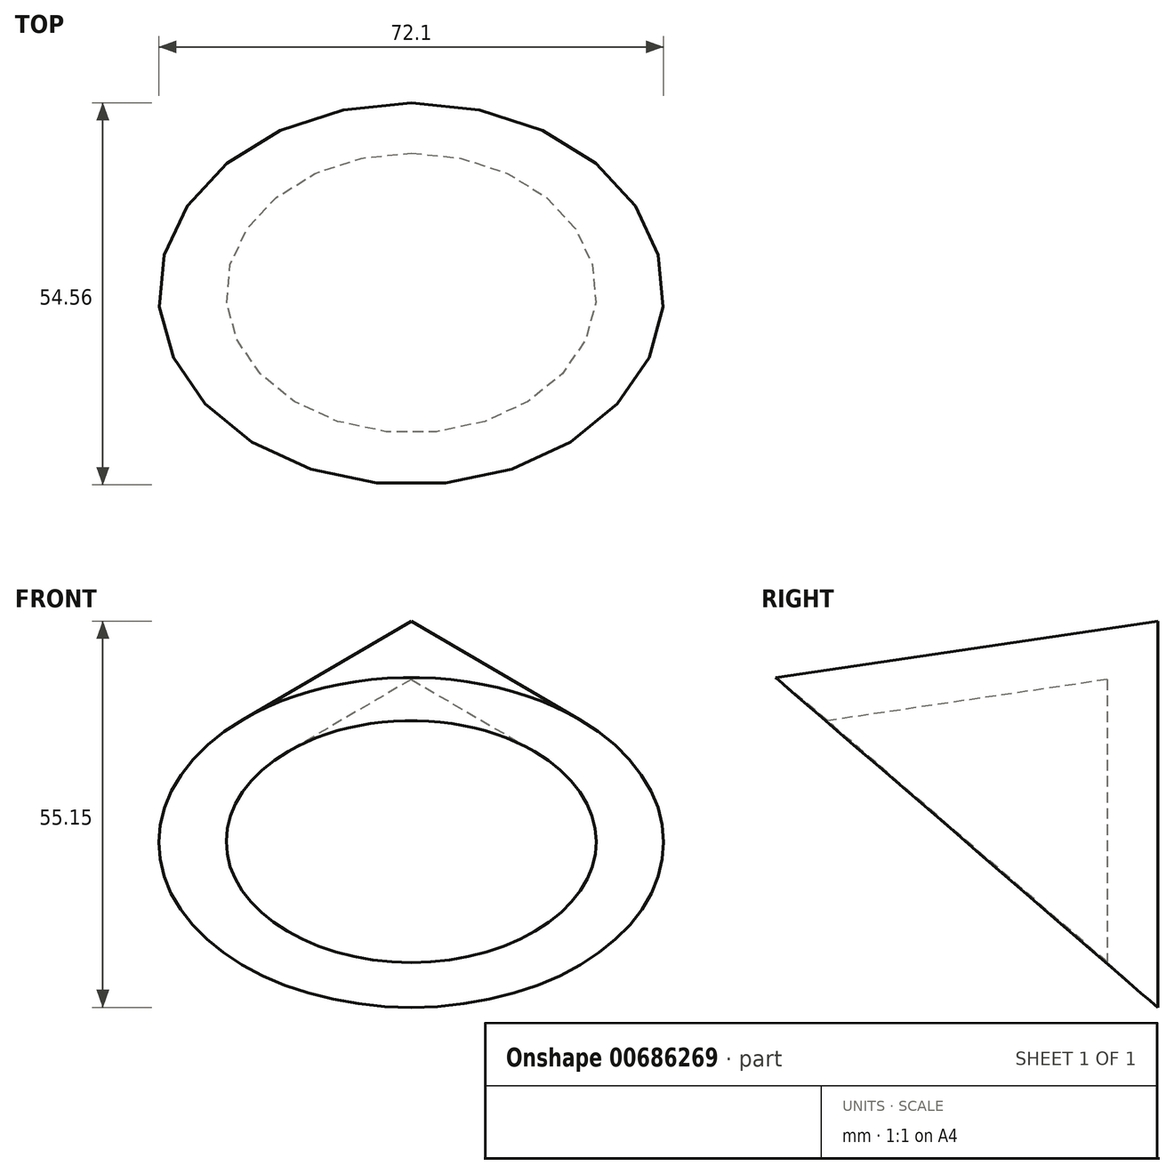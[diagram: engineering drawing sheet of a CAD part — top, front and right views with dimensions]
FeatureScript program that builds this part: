
annotation { "Feature Type Name" : "Feature", "Feature Type Description" : "" }
export const myFeature = defineFeature(function(context is Context, id is Id, definition is map)
    precondition{}
    {
        {
            var Q0;
            Q0=qCreatedBy(makeId("Right.planeOp"),FACE);
            var sketch = newSketch(context, id + "F0", { "sketchPlane" : qUnion([Q0])});
            skLineSegment(sketch, "E0", {"start": v(27, 37.22) * mm, "end": v(27, -17.93) * mm});
            skLineSegment(sketch, "E1", {"start": v(27, -17.93) * mm, "end": v(19.83, -11.5) * mm});
            skLineSegment(sketch, "E2", {"start": v(19.83, -11.5) * mm, "end": v(19.83, 28.9) * mm});
            skLineSegment(sketch, "E3", {"start": v(19.83, 28.9) * mm, "end": v(27, 37.22) * mm});
            skSolve(sketch);
        }
        {
            var Q0;
            Q0 = qSketchRegion(id + "F0", true);
            var Q1;
            Q1=sQuery(id+"F0.wireOp",EDGE,"E3");
            revolve(context, id + "F1", {"entities" : qUnion([Q0]), "axis" : qUnion([Q1]), "revolveType" : RevolveType.FULL});
        }
    });
